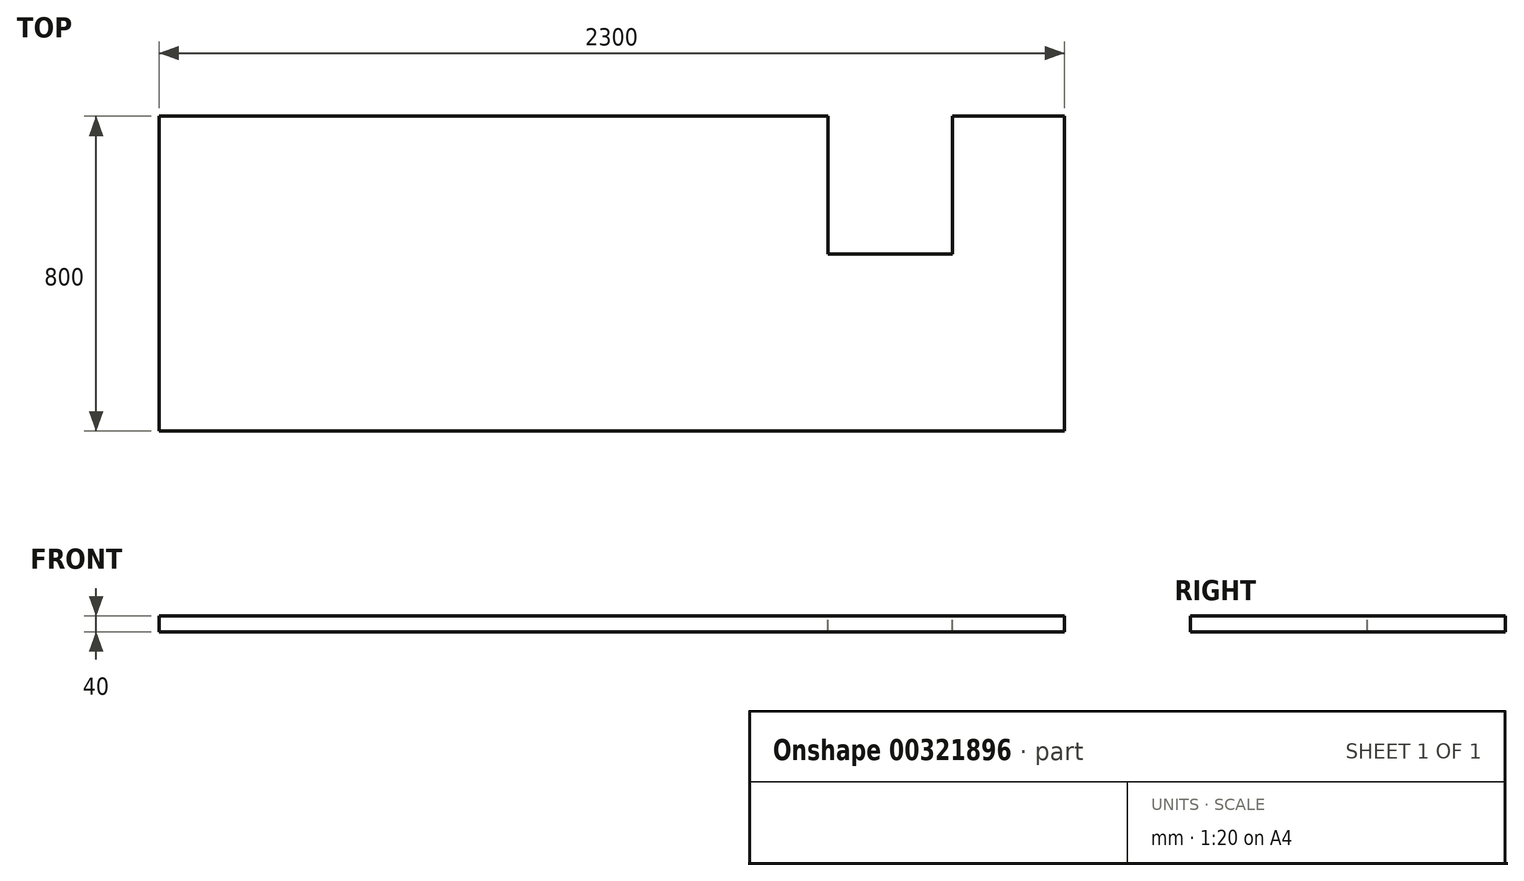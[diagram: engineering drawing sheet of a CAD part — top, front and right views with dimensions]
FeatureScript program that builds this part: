
annotation { "Feature Type Name" : "Feature", "Feature Type Description" : "" }
export const myFeature = defineFeature(function(context is Context, id is Id, definition is map)
    precondition{}
    {
        {
            var Q0;
            Q0=qCreatedBy(makeId("Top.planeOp"),FACE);
            var sketch = newSketch(context, id + "F0", { "sketchPlane" : qUnion([Q0])});
            skLineSegment(sketch, "E0.bottom", {"start": v(-92.99, 800) * mm, "end": v(2207.01, 800) * mm});
            skLineSegment(sketch, "E0.top", {"start": v(-92.99, 0) * mm, "end": v(2207.01, 0) * mm});
            skLineSegment(sketch, "E0.left", {"start": v(-92.99, 800) * mm, "end": v(-92.99, 0) * mm});
            skLineSegment(sketch, "E0.right", {"start": v(2207.01, 800) * mm, "end": v(2207.01, 0) * mm});
            skSolve(sketch);
        }
        {
            var Q0;
            Q0 = qSketchRegion(id + "F0", true);
            extrude(context, id + "F1", {"entities" : qUnion([Q0]), "depth" : 40 * mm});
        }
        {
            var Q0;
            Q0=makeQuery(id+"F1.opExtrude","CAP_FACE",FACE,{"disambiguationData":[OSD([sQuery(id+"F0.wireOp",EDGE,"E0.bottom"),sQuery(id+"F0.wireOp",EDGE,"E0.top"),sQuery(id+"F0.wireOp",EDGE,"E0.left"),sQuery(id+"F0.wireOp",EDGE,"E0.right")])],"isStart":false});
            var sketch = newSketch(context, id + "F2", { "sketchPlane" : qUnion([Q0])});
            skLineSegment(sketch, "E1", {"start": v(2207.01, 800) * mm, "end": v(1922.01, 800) * mm});
            skLineSegment(sketch, "E2.bottom", {"start": v(1922.01, 800) * mm, "end": v(1606.01, 800) * mm});
            skLineSegment(sketch, "E2.top", {"start": v(1922.01, 450) * mm, "end": v(1606.01, 450) * mm});
            skLineSegment(sketch, "E2.left", {"start": v(1922.01, 800) * mm, "end": v(1922.01, 450) * mm});
            skLineSegment(sketch, "E2.right", {"start": v(1606.01, 800) * mm, "end": v(1606.01, 450) * mm});
            skSolve(sketch);
        }
        {
            var Q0;
            Q0 = qSketchRegion(id + "F2", true);
            extrude(context, id + "F3", {"entities" : qUnion([Q0]), "operationType" : NewBodyOperationType.REMOVE, "oppositeDirection" : true, "depth" : 40 * mm});
        }
    });
